# Revit family: v-36_375k7_50Hz - コピー
name_source: partatom
category: 機械設備
units: mm (PartAtom-declared; Revit-internal decimal feet)

## family parameters
OmniClass タイトル = Centrifugal Fans
OmniClass 番号 = 23.75.35.17.27
パーツ タイプ = 標準
ロード時にボイドで切り取り = いいえ
丸型コネクタ寸法 = 直径を使用
作業面ベース = いいえ
共有 = いいえ
常に垂直 = はい
部屋計算ポイント = いいえ

## types (4) — shared parameters
D1 = 95
Depth = 580  [stored 1.90289 ft]
Duct_D = 125  [stored 0.410105 ft]
Duct_Height = 54  [stored 0.177165 ft]
Duct_Pitch = 350  [stored 1.14829 ft]
EAサイズ_D = 148  [stored 0.485564 ft]
H1 = 110  [stored 0.360892 ft]
Height = 190
IfcExportAs = IfcFanType
IfcExportType = CENTRIFUGALFORWARDCURVED
MAX静圧 = 0.0 Pa
MAX風量 = 550.0 m³/h
MID静圧 = 0.0 Pa
MID風量 = 330.0 m³/h
MIN静圧 = 0.0 Pa
MIN風量 = 200.0 m³/h
OmniClassCode = 23-33 31 19 13 15
URL = https://www.mitsubishielectric.co.jp
Uniclass2015Code = Pr_65_67_29_12
Uniclass2015Title = Centrifugal fans
Uniclass2015Version = Systems v1.9
☑給気／□排気 = いいえ
ダクト径 = 150 mm
仕様書バージョン = Version1.0
企業コード = 108420
分類コード = 50052503100060
取付金具_Depth = 6  [stored 0.019685 ft]
取付金具_H = 30  [stored 0.0984252 ft]
取付金具_ピッチ = 500  [stored 1.64042 ft]
取付金具_径 = 10  [stored 0.0328084 ft]
取付金具_穴位置 = 16  [stored 0.0524934 ft]
周波数 = 50 Hz
呼称 = 遠心送風機
外気量 = 0.0 m³/h
天吊用穴_D = 300
天吊用穴_ピッチ = 520
実風量 = 0.0 m³/h
形式 = 片吸込形
排気量 = 0.0 m³/h
極数 = 2
機外静圧 = 0.0 Pa
機外静圧_排気 = 210.0 Pa
法定耐用年数 = 15
相 = 1
積算_科目 = 2 換気設備
符号 = FE
製品リリース年月 = 2022年6月1日
製品出荷対象 = 国内
製造元 = 三菱電機株式会社
設置方法 = 天吊
設計風量 = 0.0 m³/h
説明 = レンジフードファン 浅形 高静圧・丸排気タイプ
負荷分類 = 3_ファン類
運転質量 = 0.00 kg
電動機出力 = 0 W
電圧 = 100 V
風量 = 550.0 m³/h
騒音レベル(dB(A)) = 46.5
zero-valued in all types: Clearance Back, Clearance Bottom, Clearance Front, Clearance Left, Clearance Right, Clearance Top

## per-type parameters (varying)
| type | W1 | Width | マテリアル | 価格 | 消費電力 | 製品質量 | 質量 |
| V-36K6-BL | 300 | 600  [stored 1.9685 ft] | 鋼板(白) | 87500 $ | 112 W | 15.00 kg | 18.00 kg |
| V-36K6-BL-BK | 300 | 600  [stored 1.9685 ft] | 鋼板(黒) | 87500 $ | 112 W | 15.00 kg | 18.00 kg |
| V-37KCP6 | 350  [stored 1.14829 ft] | 700  [stored 2.29659 ft] | 鋼板(白) | 97400 $ | 102 W | 16.00 kg | 19.20 kg |
| V-37KCP6-BK | 350  [stored 1.14829 ft] | 700  [stored 2.29659 ft] | 鋼板(黒) | 97400 $ | 102 W | 16.00 kg | 19.20 kg |

note: column(s) folded — value = type name in every type: モデル

note: [stored X ft] marks values corroborated as IEEE doubles in the binary element streams (Revit-internal decimal feet)

## geometry (parser evidence)
native form markers: Blend x2
no freeform markers — native parametric forms only
